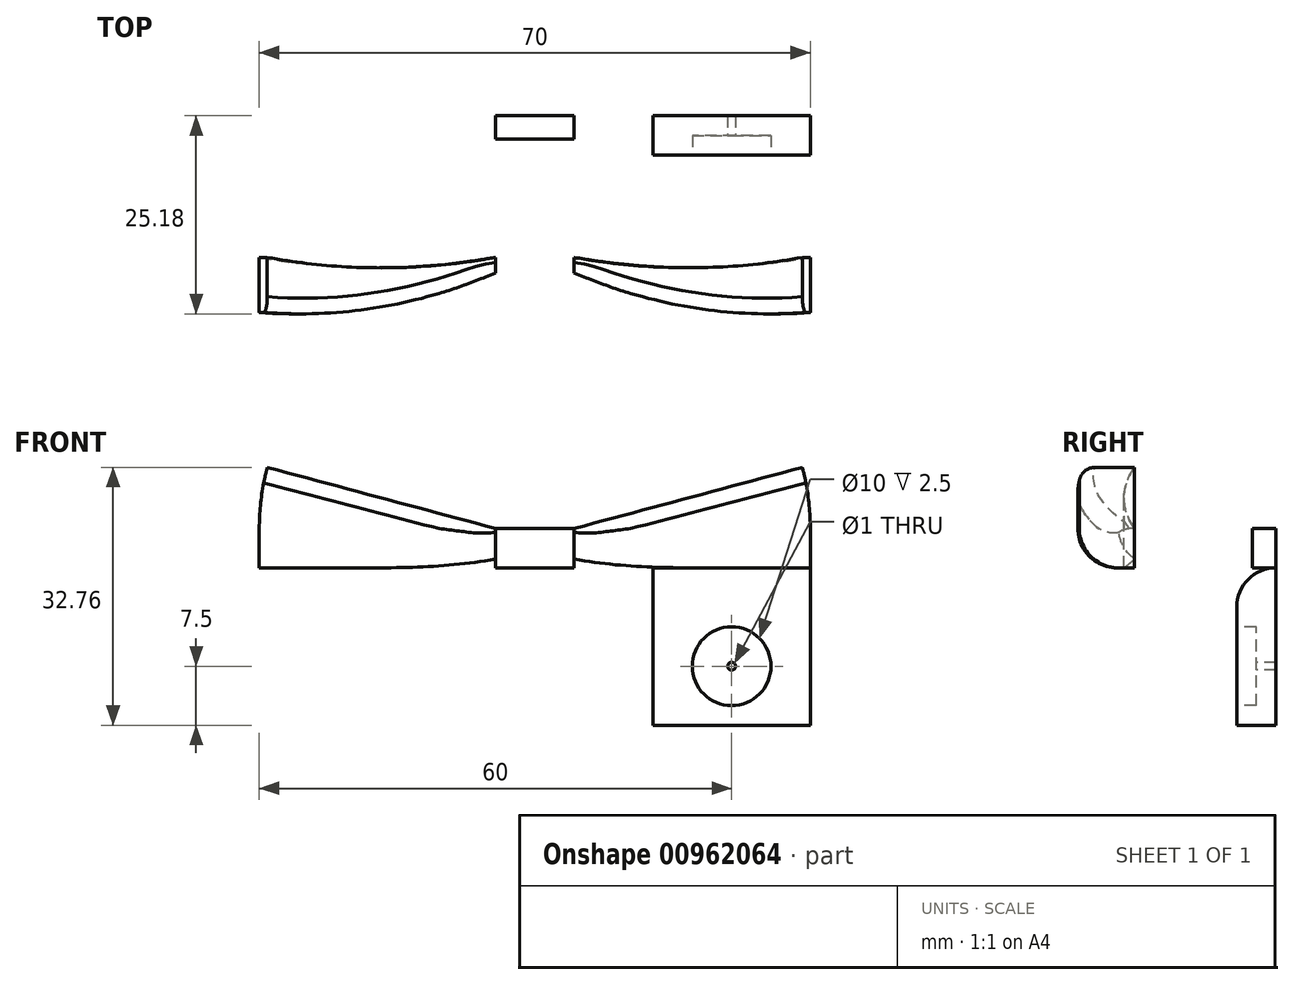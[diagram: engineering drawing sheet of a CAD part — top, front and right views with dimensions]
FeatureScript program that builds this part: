
annotation { "Feature Type Name" : "Feature", "Feature Type Description" : "" }
export const myFeature = defineFeature(function(context is Context, id is Id, definition is map)
    precondition{}
    {
        {
            var Q0;
            Q0=qCreatedBy(makeId("Top.planeOp"),FACE);
            var sketch = newSketch(context, id + "F0", { "sketchPlane" : qUnion([Q0])});
            skLineSegment(sketch, "E0", {"start": v(0, 0) * mm, "end": v(70, 0) * mm});
            skLineSegment(sketch, "E1", {"start": v(70, 0) * mm, "end": v(70, -25) * mm});
            skLineSegment(sketch, "E2", {"start": v(0, 0) * mm, "end": v(0, -25) * mm});
            skLineSegment(sketch, "E3", {"start": v(0, 0) * mm, "end": v(30, 0) * mm});
            skLineSegment(sketch, "E4", {"start": v(30, 0) * mm, "end": v(30, -20) * mm});
            skLineSegment(sketch, "E5", {"start": v(70, 0) * mm, "end": v(40, 0) * mm});
            skLineSegment(sketch, "E6", {"start": v(40, 0) * mm, "end": v(40, -20) * mm});
            skLineSegment(sketch, "E7", {"start": v(40, -3) * mm, "end": v(30, -3) * mm});
            skArc(sketch, "E8", {"start": v(0, -25) * mm, "mid": v(15.3, -24.3) * mm, "end": v(30, -20) * mm});
            skArc(sketch, "E9", {"start": v(40, -20) * mm, "mid": v(54.7, -24.3) * mm, "end": v(70, -25) * mm});
            skLineSegment(sketch, "E10", {"start": v(70, -25) * mm, "end": v(70, -18) * mm});
            skLineSegment(sketch, "E11", {"start": v(0, -25) * mm, "end": v(0, -18) * mm});
            skArc(sketch, "E12", {"start": v(0, -18) * mm, "mid": v(15, -19.33) * mm, "end": v(30, -18) * mm});
            skArc(sketch, "E13", {"start": v(40, -18) * mm, "mid": v(55, -19.32) * mm, "end": v(70, -18) * mm});
            skSolve(sketch);
        }
        {
            var Q0;
            Q0=makeQuery(id+"F0.imprint","IMPRINT",FACE,{"disambiguationData":[TD([[makeQuery(id+"F0.imprint","IMPRINT",EDGE,{"derivedFrom":sQuery(id+"F0.wireOp",EDGE,"E1")}),-1.0]])]});
            var Q1;
            {var subQ0=sQuery(id+"F0.wireOp",EDGE,"E9");Q1=makeQuery(id+"F0.imprint","IMPRINT",FACE,{"disambiguationData":[TD([[makeQuery(id+"F0.imprint","IMPRINT",EDGE,{"derivedFrom":subQ0}),1.0]])]});}
            var Q2;
            {var subQ0=sQuery(id+"F0.wireOp",EDGE,"E8");Q2=makeQuery(id+"F0.imprint","IMPRINT",FACE,{"disambiguationData":[TD([[makeQuery(id+"F0.imprint","IMPRINT",EDGE,{"derivedFrom":subQ0}),1.0]])]});}
            var Q3;
            Q3=makeQuery(id+"F0.imprint","IMPRINT",FACE,{"disambiguationData":[TD([[makeQuery(id+"F0.imprint","IMPRINT",EDGE,{"derivedFrom":sQuery(id+"F0.wireOp",EDGE,"E2")}),1.0]])]});
            var Q4;
            {var subQ0=sQuery(id+"F0.wireOp",EDGE,"E0");Q4=makeQuery(id+"F0.imprint","IMPRINT",FACE,{"disambiguationData":[TD([[makeQuery(id+"F0.imprint","IMPRINT",EDGE,{"derivedFrom":subQ0}),-1.0]])]});}
            extrude(context, id + "F1", {"entities" : qUnion([Q0, Q1, Q2, Q3, Q4]), "oppositeDirection" : true, "depth" : 5 * mm, "offsetDistance" : 25 * mm});
        }
        {
            var Q0;
            {var subQ0=sQuery(id+"F0.wireOp",EDGE,"E9");Q0=makeQuery(id+"F0.imprint","IMPRINT",FACE,{"disambiguationData":[TD([[makeQuery(id+"F0.imprint","IMPRINT",EDGE,{"derivedFrom":subQ0}),1.0]])]});}
            var Q1;
            Q1=sQuery(id+"F0.wireOp",EDGE,"E6");
            revolve(context, id + "F2", {"operationType" : NewBodyOperationType.ADD, "surfaceOperationType" : NewSurfaceOperationType.NEW, "entities" : qUnion([Q0]), "axis" : qUnion([Q1]), "revolveType" : RevolveType.ONE_DIRECTION, "angle" : 15 * degree});
        }
        {
            var Q0;
            {var subQ0=sQuery(id+"F0.wireOp",EDGE,"E8");Q0=makeQuery(id+"F0.imprint","IMPRINT",FACE,{"disambiguationData":[TD([[makeQuery(id+"F0.imprint","IMPRINT",EDGE,{"derivedFrom":subQ0}),1.0]])]});}
            var Q1;
            Q1=sQuery(id+"F0.wireOp",EDGE,"E4");
            revolve(context, id + "F3", {"operationType" : NewBodyOperationType.ADD, "surfaceOperationType" : NewSurfaceOperationType.NEW, "entities" : qUnion([Q0]), "axis" : qUnion([Q1]), "revolveType" : RevolveType.ONE_DIRECTION, "oppositeDirection" : true, "angle" : 15 * degree});
        }
        {
            var Q0;
            Q0=makeQuery(id+"F1.opExtrude","CAP_EDGE",EDGE,{"disambiguationData":[OSD([sQuery(id+"F0.wireOp",EDGE,"E8")])],"isStart":false});
            var Q1;
            Q1=makeQuery(id+"F1.opExtrude","CAP_EDGE",EDGE,{"disambiguationData":[OSD([sQuery(id+"F0.wireOp",EDGE,"E9")])],"isStart":false});
            fillet(context, id + "F4", {"entities" : qUnion([Q0, Q1]), "radius" : 5 * mm, "tangentPropagation" : true, "allowEdgeOverflow" : false});
        }
        {
            var Q0;
            Q0=makeQuery(id+"F3.opRevolve","CAP_EDGE",EDGE,{"disambiguationData":[OSD([sQuery(id+"F0.wireOp",EDGE,"E11")])],"isStart":false});
            var Q1;
            Q1=makeQuery(id+"F3.opRevolve","CAP_EDGE",EDGE,{"disambiguationData":[OSD([sQuery(id+"F0.wireOp",EDGE,"E8")])],"isStart":false});
            var Q2;
            Q2=makeQuery(id+"F2.opRevolve","CAP_EDGE",EDGE,{"disambiguationData":[OSD([sQuery(id+"F0.wireOp",EDGE,"E9")])],"isStart":false});
            var Q3;
            Q3=makeQuery(id+"F2.opRevolve","CAP_EDGE",EDGE,{"disambiguationData":[OSD([sQuery(id+"F0.wireOp",EDGE,"E10")])],"isStart":false});
            fillet(context, id + "F5", {"entities" : qUnion([Q0, Q1, Q2, Q3]), "radius" : 2 * mm, "tangentPropagation" : true, "allowEdgeOverflow" : false});
        }
        {
            var Q0;
            Q0=makeQuery(id+"F1.opExtrude","CAP_FACE",FACE,{"disambiguationData":[OSD([sQuery(id+"F0.wireOp",EDGE,"E0"),sQuery(id+"F0.wireOp",EDGE,"E1"),sQuery(id+"F0.wireOp",EDGE,"E2"),sQuery(id+"F0.wireOp",EDGE,"E3"),sQuery(id+"F0.wireOp",EDGE,"E4"),sQuery(id+"F0.wireOp",EDGE,"E5"),sQuery(id+"F0.wireOp",EDGE,"E6"),sQuery(id+"F0.wireOp",EDGE,"E7"),sQuery(id+"F0.wireOp",EDGE,"E8"),sQuery(id+"F0.wireOp",EDGE,"E9"),sQuery(id+"F0.wireOp",EDGE,"E10"),sQuery(id+"F0.wireOp",EDGE,"E11")])],"isStart":false});
            var sketch = newSketch(context, id + "F6", { "sketchPlane" : qUnion([Q0])});
            skLineSegment(sketch, "E14", {"start": v(0, 5) * mm, "end": v(20.66, 5) * mm});
            skLineSegment(sketch, "E15", {"start": v(20.66, 5) * mm, "end": v(20.66, 0) * mm});
            skLineSegment(sketch, "E16.bottom", {"start": v(70, 0) * mm, "end": v(50, 0) * mm});
            skLineSegment(sketch, "E16.top", {"start": v(70, 5) * mm, "end": v(50, 5) * mm});
            skLineSegment(sketch, "E16.left", {"start": v(70, 0) * mm, "end": v(70, 5) * mm});
            skLineSegment(sketch, "E16.right", {"start": v(50, 0) * mm, "end": v(50, 5) * mm});
            skSolve(sketch);
        }
        {
            var Q0;
            {var subQ0=sQuery(id+"F6.wireOp",EDGE,"E14");Q0=makeQuery(id+"F6.imprint","IMPRINT",FACE,{"disambiguationData":[TD([[makeQuery(id+"F6.imprint","IMPRINT",EDGE,{"derivedFrom":subQ0}),-1.0]])]});}
            var Q1;
            Q1=makeQuery(id+"F6.imprint","IMPRINT",FACE,{"disambiguationData":[TD([[makeQuery(id+"F6.imprint","IMPRINT",EDGE,{"derivedFrom":sQuery(id+"F6.wireOp",EDGE,"E16.bottom")}),-1.0]])]});
            extrude(context, id + "F7", {"entities" : qUnion([Q0, Q1]), "operationType" : NewBodyOperationType.ADD, "depth" : 20 * mm, "offsetDistance" : 25 * mm});
        }
        {
            var Q0;
            Q0=makeQuery(id+"F7.opExtrude","CAP_EDGE",EDGE,{"disambiguationData":[OSD([sQuery(id+"F6.wireOp",EDGE,"E14")])],"isStart":true});
            var Q1;
            Q1=makeQuery(id+"F7.opExtrude","CAP_EDGE",EDGE,{"disambiguationData":[OSD([sQuery(id+"F6.wireOp",EDGE,"E16.top")])],"isStart":true});
            fillet(context, id + "F8", {"entities" : qUnion([Q0, Q1]), "radius" : 5 * mm, "tangentPropagation" : true, "allowEdgeOverflow" : false});
        }
        {
            var Q0;
            Q0=makeQuery(id+"F7.opExtrude","SWEPT_FACE",FACE,{"disambiguationData":[OSD([sQuery(id+"F6.wireOp",EDGE,"E14")])]});
            var sketch = newSketch(context, id + "F9", { "sketchPlane" : qUnion([Q0])});
            skLineSegment(sketch, "E17", {"start": v(10.33, -25) * mm, "end": v(10.33, -10) * mm});
            skLineSegment(sketch, "E18", {"start": v(10.33, -17.5) * mm, "end": v(0, -17.5) * mm});
            skLineSegment(sketch, "E19", {"start": v(10.33, -17.5) * mm, "end": v(20.66, -17.5) * mm});
            skCircle(sketch, "E20", {"center": v(10.33, -17.5) * mm, "radius": 5 * mm});
            skSolve(sketch);
        }
        {
            var Q0;
            Q0=makeQuery(id+"F7.opExtrude","SWEPT_FACE",FACE,{"disambiguationData":[OSD([sQuery(id+"F6.wireOp",EDGE,"E16.top")])]});
            var sketch = newSketch(context, id + "F10", { "sketchPlane" : qUnion([Q0])});
            skCircle(sketch, "E21", {"center": v(60, -17.5) * mm, "radius": 5 * mm});
            skPoint(sketch, "E21.centerSnap0", {"position": v(50, -17.5) * mm});
            skPoint(sketch, "E21.centerSnap1", {"position": v(60, -25) * mm});
            skSolve(sketch);
        }
        {
            var Q0;
            {var subQ1=sQuery(id+"F9.wireOp",EDGE,"E17");var subQ3=sQuery(id+"F9.wireOp",EDGE,"E20");var subQ4=makeQuery(id+"F9.imprint","INTERSECT",VERTEX,{"disambiguationData":[OD(1.0)],"derivedFrom":[subQ1,subQ3]});Q0=makeQuery(id+"F9.imprint","IMPRINT",FACE,{"disambiguationData":[TD([[makeQuery(id+"F9.imprint","IMPRINT",EDGE,{"disambiguationData":[TD([[subQ4,1.0]])],"derivedFrom":subQ3}),1.0]])]});}
            var Q1;
            {var subQ1=sQuery(id+"F9.wireOp",EDGE,"E17");var subQ3=sQuery(id+"F9.wireOp",EDGE,"E20");var subQ4=makeQuery(id+"F9.imprint","INTERSECT",VERTEX,{"disambiguationData":[OD(1.0)],"derivedFrom":[subQ1,subQ3]});Q1=makeQuery(id+"F9.imprint","IMPRINT",FACE,{"disambiguationData":[TD([[makeQuery(id+"F9.imprint","IMPRINT",EDGE,{"disambiguationData":[TD([[subQ4,-1.0]])],"derivedFrom":subQ3}),1.0]])]});}
            var Q2;
            {var subQ1=sQuery(id+"F9.wireOp",EDGE,"E17");var subQ3=sQuery(id+"F9.wireOp",EDGE,"E20");var subQ4=makeQuery(id+"F9.imprint","INTERSECT",VERTEX,{"disambiguationData":[OD(0.0)],"derivedFrom":[subQ1,subQ3]});Q2=makeQuery(id+"F9.imprint","IMPRINT",FACE,{"disambiguationData":[TD([[makeQuery(id+"F9.imprint","IMPRINT",EDGE,{"disambiguationData":[TD([[subQ4,1.0]])],"derivedFrom":subQ3}),1.0]])]});}
            var Q3;
            {var subQ1=sQuery(id+"F9.wireOp",EDGE,"E17");var subQ3=sQuery(id+"F9.wireOp",EDGE,"E20");var subQ4=makeQuery(id+"F9.imprint","INTERSECT",VERTEX,{"disambiguationData":[OD(0.0)],"derivedFrom":[subQ1,subQ3]});Q3=makeQuery(id+"F9.imprint","IMPRINT",FACE,{"disambiguationData":[TD([[makeQuery(id+"F9.imprint","IMPRINT",EDGE,{"disambiguationData":[TD([[subQ4,-1.0]])],"derivedFrom":subQ3}),1.0]])]});}
            var Q4;
            Q4=makeQuery(id+"F10.imprint","IMPRINT",FACE,{"disambiguationData":[TD([[makeQuery(id+"F10.imprint","IMPRINT",EDGE,{"derivedFrom":sQuery(id+"F10.wireOp",EDGE,"E21")}),1.0]])]});
            extrude(context, id + "F11", {"entities" : qUnion([Q0, Q1, Q2, Q3, Q4]), "operationType" : NewBodyOperationType.REMOVE, "oppositeDirection" : true, "depth" : 2.5 * mm, "offsetDistance" : 25 * mm});
        }
        {
            var Q0;
            Q0=makeQuery(id+"F11.boolean.opBoolean","COPY",FACE,{"derivedFrom":makeQuery(id+"F11.opExtrude","CAP_FACE",FACE,{"disambiguationData":[OSD([sQuery(id+"F9.wireOp",EDGE,"E20")])],"isStart":false})});
            var sketch = newSketch(context, id + "F12", { "sketchPlane" : qUnion([Q0])});
            skCircle(sketch, "E22", {"center": v(10.33, -17.5) * mm, "radius": 0.5 * mm});
            skSolve(sketch);
        }
        {
            var Q0;
            Q0=makeQuery(id+"F11.boolean.opBoolean","COPY",FACE,{"derivedFrom":makeQuery(id+"F11.opExtrude","CAP_FACE",FACE,{"disambiguationData":[OSD([sQuery(id+"F10.wireOp",EDGE,"E21")])],"isStart":false})});
            var sketch = newSketch(context, id + "F13", { "sketchPlane" : qUnion([Q0])});
            skCircle(sketch, "E23", {"center": v(60, -17.5) * mm, "radius": 0.5 * mm});
            skSolve(sketch);
        }
        {
            var Q0;
            Q0=makeQuery(id+"F12.imprint","IMPRINT",FACE,{"disambiguationData":[TD([[makeQuery(id+"F12.imprint","IMPRINT",EDGE,{"derivedFrom":sQuery(id+"F12.wireOp",EDGE,"E22")}),1.0]])]});
            var Q1;
            Q1=makeQuery(id+"F13.imprint","IMPRINT",FACE,{"disambiguationData":[TD([[makeQuery(id+"F13.imprint","IMPRINT",EDGE,{"derivedFrom":sQuery(id+"F13.wireOp",EDGE,"E23")}),1.0]])]});
            extrude(context, id + "F14", {"entities" : qUnion([Q0, Q1]), "operationType" : NewBodyOperationType.REMOVE, "oppositeDirection" : true, "depth" : 25 * mm, "offsetDistance" : 25 * mm});
        }
    });
